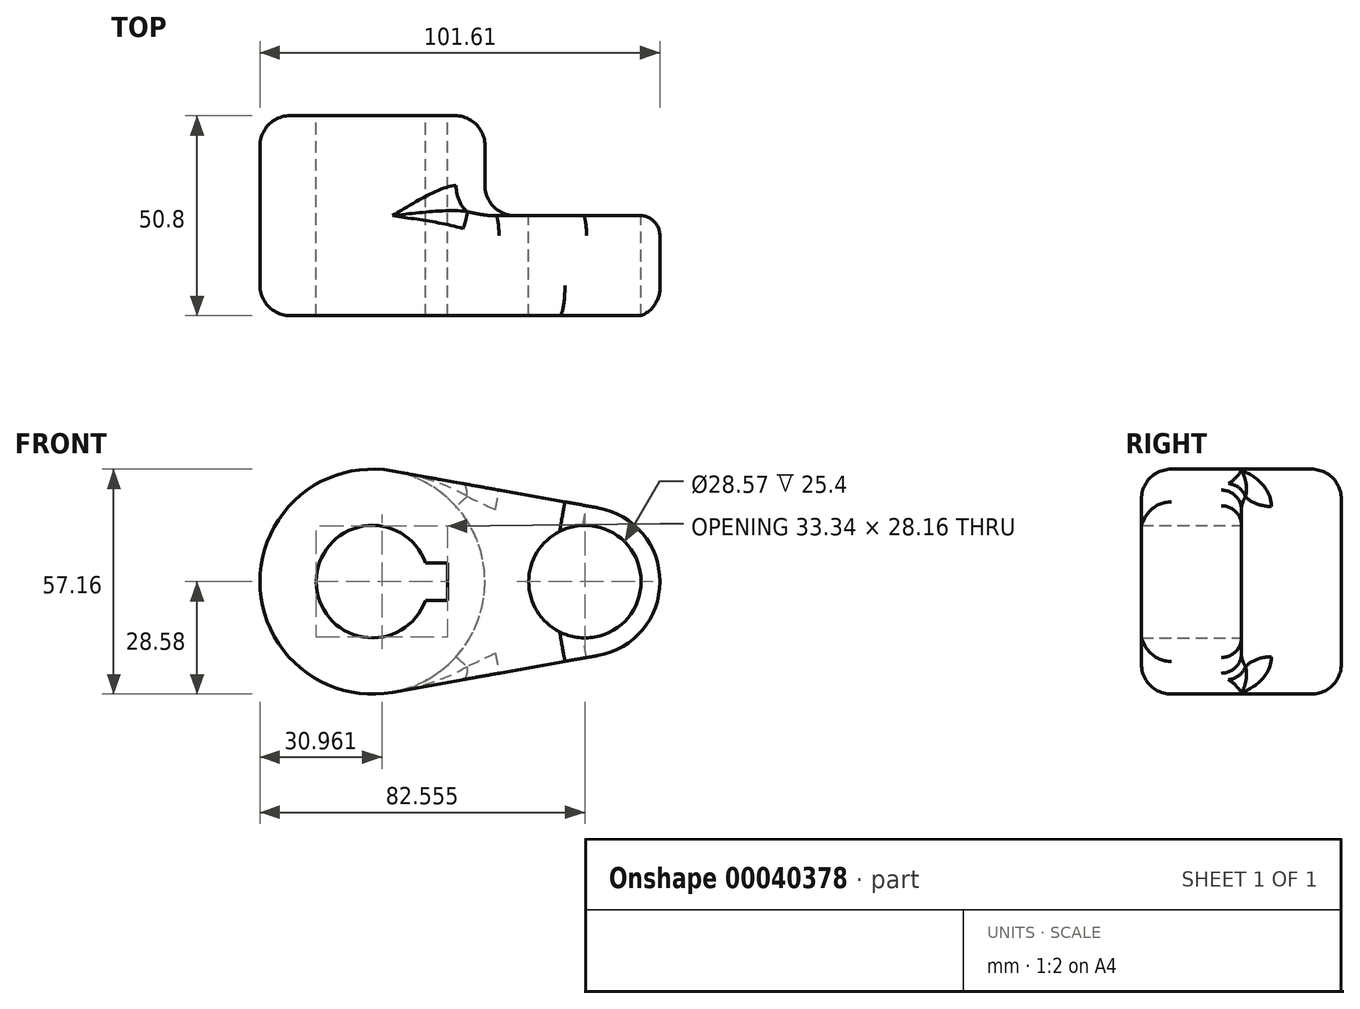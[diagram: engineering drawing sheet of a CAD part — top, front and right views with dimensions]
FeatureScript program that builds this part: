
annotation { "Feature Type Name" : "Feature", "Feature Type Description" : "" }
export const myFeature = defineFeature(function(context is Context, id is Id, definition is map)
    precondition{}
    {
        {
            var Q0;
            Q0=qCreatedBy(makeId("Front.planeOp"),FACE);
            var sketch = newSketch(context, id + "F0", { "sketchPlane" : qUnion([Q0])});
            skCircle(sketch, "E0", {"center": v(0, 0) * mm, "radius": 28.57 * mm});
            skCircle(sketch, "E1", {"center": v(53.98, 0) * mm, "radius": 19.05 * mm});
            skLineSegment(sketch, "E2", {"start": v(5.04, 28.13) * mm, "end": v(57.34, 18.75) * mm});
            skLineSegment(sketch, "E3", {"start": v(5.04, -28.13) * mm, "end": v(57.34, -18.75) * mm});
            skCircle(sketch, "E4", {"center": v(0, 0) * mm, "radius": 14.29 * mm});
            skCircle(sketch, "E5", {"center": v(53.98, 0) * mm, "radius": 14.29 * mm});
            skLineSegment(sketch, "E6.rect.bottom", {"start": v(-19.05, 4.76) * mm, "end": v(19.05, 4.76) * mm});
            skLineSegment(sketch, "E6.rect.top", {"start": v(-19.05, -4.76) * mm, "end": v(19.05, -4.76) * mm});
            skLineSegment(sketch, "E6.rect.left", {"start": v(-19.05, 4.76) * mm, "end": v(-19.05, -4.76) * mm});
            skLineSegment(sketch, "E6.rect.right", {"start": v(19.05, 4.76) * mm, "end": v(19.05, -4.76) * mm});
            skSolve(sketch);
        }
        {
            var Q0;
            {var subQ5=sQuery(id+"F0.wireOp",EDGE,"E6.rect.left");Q0=makeQuery(id+"F0.imprint","IMPRINT",FACE,{"disambiguationData":[TD([[makeQuery(id+"F0.imprint","IMPRINT",EDGE,{"derivedFrom":subQ5}),-1.0]])]});}
            var Q1;
            {var subQ0=sQuery(id+"F0.wireOp",EDGE,"E6.rect.left");Q1=makeQuery(id+"F0.imprint","IMPRINT",FACE,{"disambiguationData":[TD([[makeQuery(id+"F0.imprint","IMPRINT",EDGE,{"derivedFrom":subQ0}),1.0]])]});}
            var Q2;
            {var subQ1=sQuery(id+"F0.wireOp",EDGE,"E2");Q2=makeQuery(id+"F0.imprint","IMPRINT",FACE,{"disambiguationData":[TD([[makeQuery(id+"F0.imprint","IMPRINT",EDGE,{"derivedFrom":subQ1}),-1.0]])]});}
            var Q3;
            Q3=makeQuery(id+"F0.imprint","IMPRINT",FACE,{"disambiguationData":[TD([[makeQuery(id+"F0.imprint","IMPRINT",EDGE,{"derivedFrom":sQuery(id+"F0.wireOp",EDGE,"E5")}),-1.0]])]});
            extrude(context, id + "F1", {"entities" : qUnion([Q0, Q1, Q2, Q3]), "depth" : 25.4 * mm});
        }
        {
            var Q0;
            {var subQ5=sQuery(id+"F0.wireOp",EDGE,"E6.rect.left");Q0=makeQuery(id+"F0.imprint","IMPRINT",FACE,{"disambiguationData":[TD([[makeQuery(id+"F0.imprint","IMPRINT",EDGE,{"derivedFrom":subQ5}),-1.0]])]});}
            var Q1;
            {var subQ0=sQuery(id+"F0.wireOp",EDGE,"E6.rect.left");Q1=makeQuery(id+"F0.imprint","IMPRINT",FACE,{"disambiguationData":[TD([[makeQuery(id+"F0.imprint","IMPRINT",EDGE,{"derivedFrom":subQ0}),1.0]])]});}
            extrude(context, id + "F2", {"entities" : qUnion([Q0, Q1]), "operationType" : NewBodyOperationType.ADD, "oppositeDirection" : true, "depth" : 25.4 * mm});
        }
        {
            var Q0;
            {var subQ0=sQuery(id+"F0.wireOp",EDGE,"E0");Q0=makeQuery(id+"F2.boolean.opBoolean","MERGE",FACE,{"derivedFrom":[makeQuery(id+"F1.opExtrude","SWEPT_FACE",FACE,{"disambiguationData":[OSD([subQ0])]}),makeQuery(id+"F2.opExtrude","SWEPT_FACE",FACE,{"disambiguationData":[OSD([subQ0])]})]});}
            fillet(context, id + "F3", {"entities" : qUnion([Q0]), "radius" : 7.62 * mm, "tangentPropagation" : true, "allowEdgeOverflow" : false});
        }
        {
            var Q0;
            Q0=makeQuery(id+"F1.opExtrude","CAP_EDGE",EDGE,{"disambiguationData":[OSD([sQuery(id+"F0.wireOp",EDGE,"E3")])],"isStart":true});
            fillet(context, id + "F4", {"entities" : qUnion([Q0]), "radius" : 5.08 * mm, "tangentPropagation" : true, "allowEdgeOverflow" : false});
        }
    });
